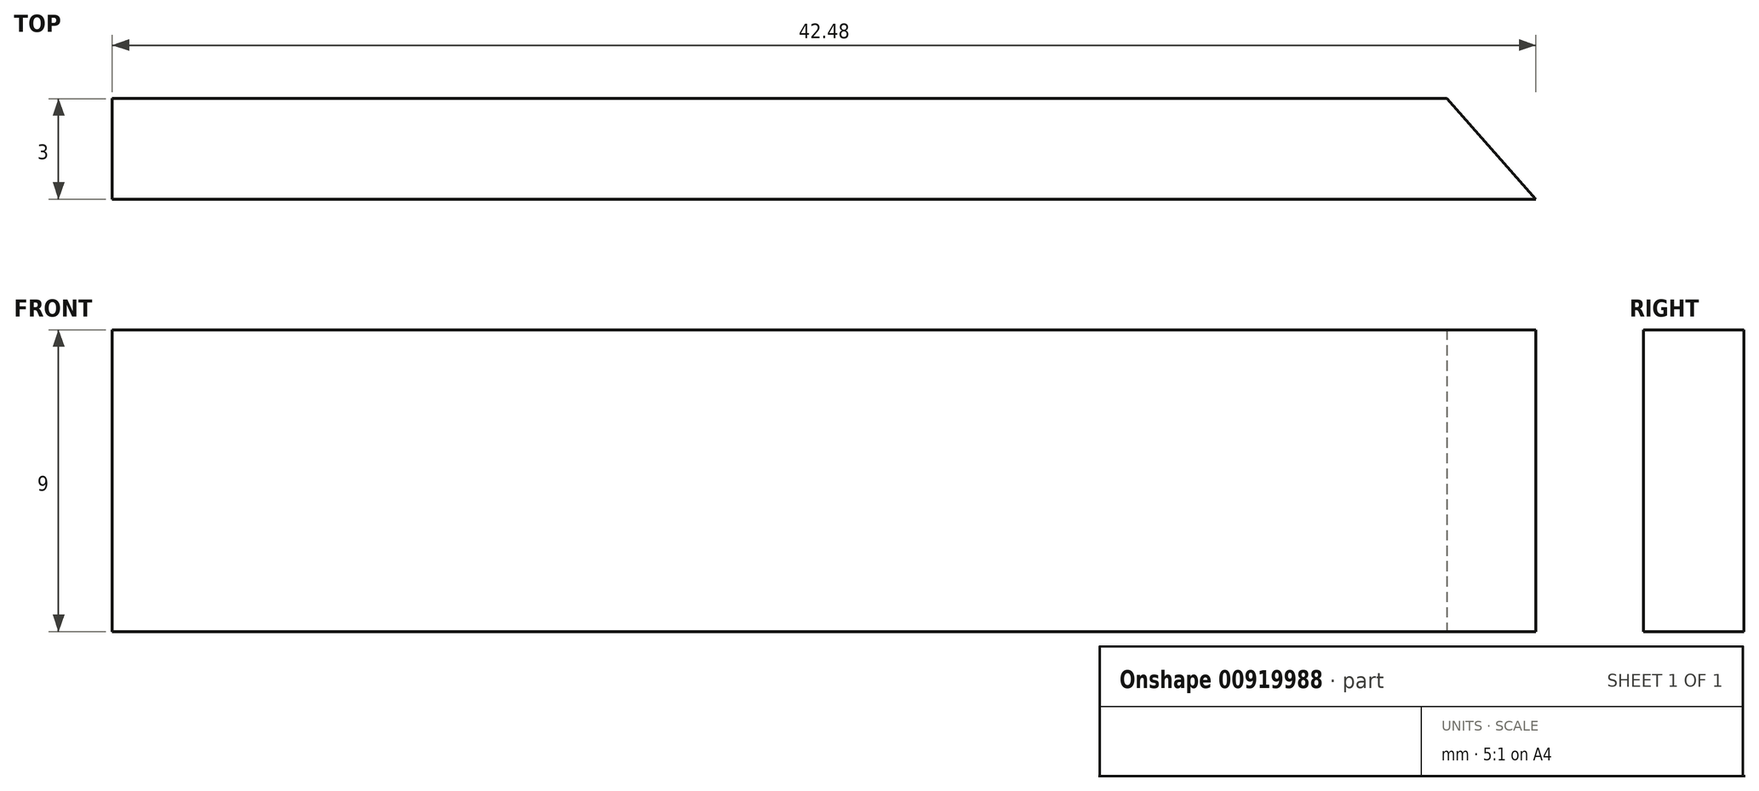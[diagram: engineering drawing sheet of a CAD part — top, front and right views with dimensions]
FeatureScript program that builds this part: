
annotation { "Feature Type Name" : "Feature", "Feature Type Description" : "" }
export const myFeature = defineFeature(function(context is Context, id is Id, definition is map)
    precondition{}
    {
        {
            var Q0;
            Q0=qCreatedBy(makeId("Top.planeOp"),FACE);
            var sketch = newSketch(context, id + "F0", { "sketchPlane" : qUnion([Q0])});
            skLineSegment(sketch, "E0", {"start": v(-46.66, 19.68) * mm, "end": v(-6.84, 19.68) * mm});
            skLineSegment(sketch, "E1", {"start": v(-6.84, 19.68) * mm, "end": v(-4.18, 16.68) * mm});
            skLineSegment(sketch, "E2", {"start": v(-4.18, 16.68) * mm, "end": v(-46.66, 16.68) * mm});
            skLineSegment(sketch, "E3", {"start": v(-46.66, 16.68) * mm, "end": v(-46.66, 19.68) * mm});
            skSolve(sketch);
        }
        {
            var Q0;
            Q0=makeQuery(id+"F0.imprint","IMPRINT",FACE,{"disambiguationData":[TD([[makeQuery(id+"F0.imprint","IMPRINT",EDGE,{"derivedFrom":sQuery(id+"F0.wireOp",EDGE,"E0")}),-1.0]])]});
            extrude(context, id + "F1", {"entities" : qUnion([Q0]), "depth" : 9 * mm, "offsetDistance" : 25 * mm});
        }
    });
